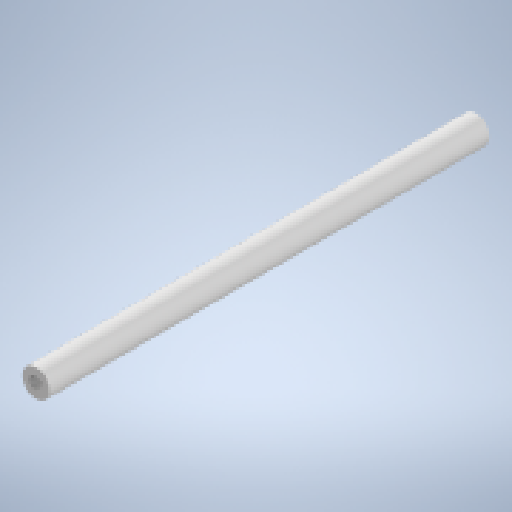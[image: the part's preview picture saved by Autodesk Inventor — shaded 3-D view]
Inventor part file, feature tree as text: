
AUTODESK INVENTOR PART (.ipt)
format: ipt  version: 2023 (Build 270158000, 158)  size: 155,648 bytes
history: native  units: mm
features: extrude x3, sketch x3, thread x2
ambient origin geometry x8: Origin, YZ Plane, XZ Plane, XY Plane, X Axis, Y Axis, Z Axis, Center Point
bodies: Solid1 (feature_tree)
feature tree (8):
  extrude  "Extrusion1"  Depth=75.0mm TaperAngle=0.0deg
  extrude  "Extrusion2"  Depth=20.0mm TaperAngle=0.0deg
  extrude  "Extrusion3"  Depth=20.0mm TaperAngle=0.0deg
  thread  "Thread1"  [1 undecoded]
  thread  "Thread2"  [1 undecoded]
  sketch  "Sketch1"  dims[d0=5.0mm d1=75.0mm d2=0.0mm]
  sketch  "Sketch2"  dims[d3=2.2mm d4=20.0mm d5=0.0mm]
  sketch  "Sketch3"  dims[d6=20.0mm d7=0.0mm d8=16.0mm d9=0.0mm d10=16.0mm d11=0.0mm]
note: 2 required parameter values undecoded (feature->parameter linkage not recoverable at this tier; creation-order binding heuristic only, values carry confidence <= 0.55)
